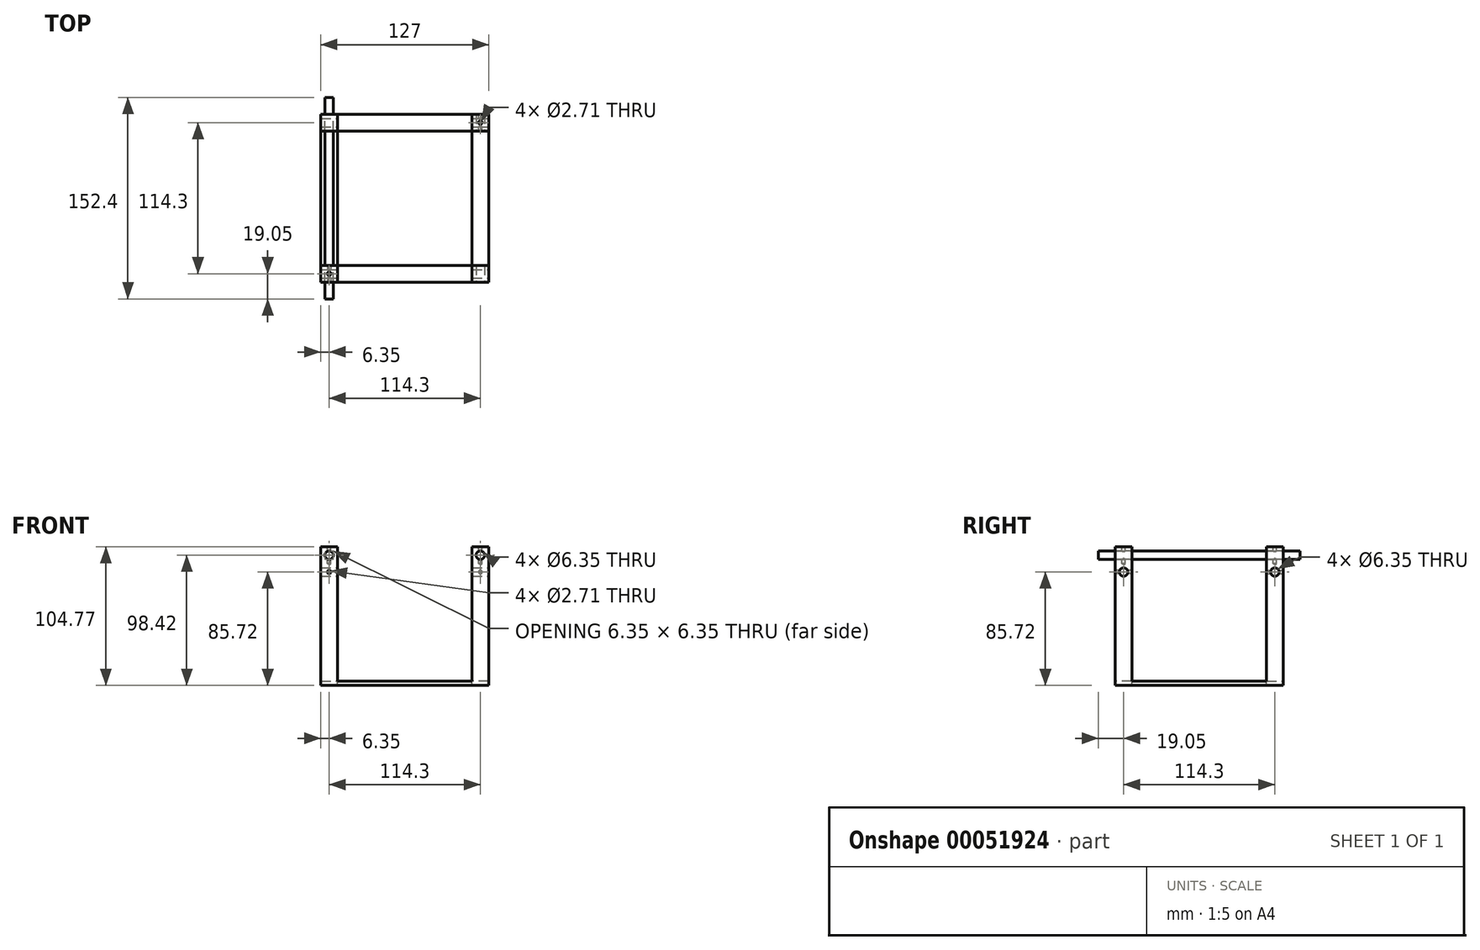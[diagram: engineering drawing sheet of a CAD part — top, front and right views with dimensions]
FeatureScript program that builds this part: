
annotation { "Feature Type Name" : "Feature", "Feature Type Description" : "" }
export const myFeature = defineFeature(function(context is Context, id is Id, definition is map)
    precondition{}
    {
        {
            var Q0;
            Q0=qCreatedBy(makeId("Top.planeOp"),FACE);
            var sketch = newSketch(context, id + "F0", { "sketchPlane" : qUnion([Q0])});
            skLineSegment(sketch, "E0.bottom", {"start": v(57.15, -57.15) * mm, "end": v(-57.15, -57.15) * mm, "construction": true});
            skLineSegment(sketch, "E0.top", {"start": v(57.15, 57.15) * mm, "end": v(-57.15, 57.15) * mm, "construction": true});
            skLineSegment(sketch, "E0.left", {"start": v(57.15, -57.15) * mm, "end": v(57.15, 57.15) * mm, "construction": true});
            skLineSegment(sketch, "E0.right", {"start": v(-57.15, -57.15) * mm, "end": v(-57.15, 57.15) * mm, "construction": true});
            skPoint(sketch, "E0.middle", {"position": v(0, 0) * mm});
            skLineSegment(sketch, "E1.bottom", {"start": v(-50.8, 50.8) * mm, "end": v(-63.5, 50.8) * mm});
            skLineSegment(sketch, "E1.top", {"start": v(-50.8, 63.5) * mm, "end": v(-63.5, 63.5) * mm});
            skLineSegment(sketch, "E1.left", {"start": v(-50.8, 50.8) * mm, "end": v(-50.8, 63.5) * mm});
            skLineSegment(sketch, "E1.right", {"start": v(-63.5, 50.8) * mm, "end": v(-63.5, 63.5) * mm});
            skPoint(sketch, "E1.middle", {"position": v(-57.15, 57.15) * mm});
            skLineSegment(sketch, "E2.bottom", {"start": v(63.5, 50.8) * mm, "end": v(50.8, 50.8) * mm});
            skLineSegment(sketch, "E2.top", {"start": v(63.5, 63.5) * mm, "end": v(50.8, 63.5) * mm});
            skLineSegment(sketch, "E2.left", {"start": v(63.5, 50.8) * mm, "end": v(63.5, 63.5) * mm});
            skLineSegment(sketch, "E2.right", {"start": v(50.8, 50.8) * mm, "end": v(50.8, 63.5) * mm});
            skPoint(sketch, "E2.middle", {"position": v(57.15, 57.15) * mm});
            skLineSegment(sketch, "E3.bottom", {"start": v(63.5, -50.8) * mm, "end": v(50.8, -50.8) * mm});
            skLineSegment(sketch, "E3.top", {"start": v(63.5, -63.5) * mm, "end": v(50.8, -63.5) * mm});
            skLineSegment(sketch, "E3.left", {"start": v(63.5, -50.8) * mm, "end": v(63.5, -63.5) * mm});
            skLineSegment(sketch, "E3.right", {"start": v(50.8, -50.8) * mm, "end": v(50.8, -63.5) * mm});
            skPoint(sketch, "E3.middle", {"position": v(57.15, -57.15) * mm});
            skLineSegment(sketch, "E4.bottom", {"start": v(-63.5, -50.8) * mm, "end": v(-50.8, -50.8) * mm});
            skLineSegment(sketch, "E4.top", {"start": v(-63.5, -63.5) * mm, "end": v(-50.8, -63.5) * mm});
            skLineSegment(sketch, "E4.left", {"start": v(-63.5, -50.8) * mm, "end": v(-63.5, -63.5) * mm});
            skLineSegment(sketch, "E4.right", {"start": v(-50.8, -50.8) * mm, "end": v(-50.8, -63.5) * mm});
            skPoint(sketch, "E4.middle", {"position": v(-57.15, -57.15) * mm});
            skLineSegment(sketch, "E5", {"start": v(-50.8, 63.5) * mm, "end": v(50.8, 63.5) * mm});
            skLineSegment(sketch, "E6", {"start": v(-50.8, 50.8) * mm, "end": v(50.8, 50.8) * mm});
            skLineSegment(sketch, "E7", {"start": v(50.8, 50.8) * mm, "end": v(50.8, -50.8) * mm});
            skLineSegment(sketch, "E8", {"start": v(63.5, 50.8) * mm, "end": v(63.5, -50.8) * mm});
            skLineSegment(sketch, "E9", {"start": v(50.8, -50.8) * mm, "end": v(-50.8, -50.8) * mm});
            skLineSegment(sketch, "E10", {"start": v(50.8, -63.5) * mm, "end": v(-50.8, -63.5) * mm});
            skLineSegment(sketch, "E11", {"start": v(-50.8, -50.8) * mm, "end": v(-50.8, 50.8) * mm});
            skLineSegment(sketch, "E12", {"start": v(-63.5, -50.8) * mm, "end": v(-63.5, 50.8) * mm});
            skSolve(sketch);
        }
        {
            var Q0;
            Q0=makeQuery(id+"F0.imprint","IMPRINT",FACE,{"disambiguationData":[TD([[makeQuery(id+"F0.imprint","IMPRINT",EDGE,{"derivedFrom":sQuery(id+"F0.wireOp",EDGE,"E4.bottom")}),-1.0]])]});
            var Q1;
            Q1=makeQuery(id+"F0.imprint","IMPRINT",FACE,{"disambiguationData":[TD([[makeQuery(id+"F0.imprint","IMPRINT",EDGE,{"derivedFrom":sQuery(id+"F0.wireOp",EDGE,"E1.bottom")}),1.0]])]});
            var Q2;
            Q2=makeQuery(id+"F0.imprint","IMPRINT",FACE,{"disambiguationData":[TD([[makeQuery(id+"F0.imprint","IMPRINT",EDGE,{"derivedFrom":sQuery(id+"F0.wireOp",EDGE,"E1.bottom")}),-1.0]])]});
            var Q3;
            Q3=makeQuery(id+"F0.imprint","IMPRINT",FACE,{"disambiguationData":[TD([[makeQuery(id+"F0.imprint","IMPRINT",EDGE,{"derivedFrom":sQuery(id+"F0.wireOp",EDGE,"E1.left")}),-1.0]])]});
            var Q4;
            Q4=makeQuery(id+"F0.imprint","IMPRINT",FACE,{"disambiguationData":[TD([[makeQuery(id+"F0.imprint","IMPRINT",EDGE,{"derivedFrom":sQuery(id+"F0.wireOp",EDGE,"E2.bottom")}),-1.0]])]});
            var Q5;
            Q5=makeQuery(id+"F0.imprint","IMPRINT",FACE,{"disambiguationData":[TD([[makeQuery(id+"F0.imprint","IMPRINT",EDGE,{"derivedFrom":sQuery(id+"F0.wireOp",EDGE,"E2.bottom")}),1.0]])]});
            var Q6;
            Q6=makeQuery(id+"F0.imprint","IMPRINT",FACE,{"disambiguationData":[TD([[makeQuery(id+"F0.imprint","IMPRINT",EDGE,{"derivedFrom":sQuery(id+"F0.wireOp",EDGE,"E3.bottom")}),1.0]])]});
            var Q7;
            Q7=makeQuery(id+"F0.imprint","IMPRINT",FACE,{"disambiguationData":[TD([[makeQuery(id+"F0.imprint","IMPRINT",EDGE,{"derivedFrom":sQuery(id+"F0.wireOp",EDGE,"E3.right")}),-1.0]])]});
            extrude(context, id + "F1", {"entities" : qUnion([Q0, Q1, Q2, Q3, Q4, Q5, Q6, Q7]), "oppositeDirection" : true, "depth" : 3.17 * mm});
        }
        {
            var Q0;
            Q0=makeQuery(id+"F0.imprint","IMPRINT",FACE,{"disambiguationData":[TD([[makeQuery(id+"F0.imprint","IMPRINT",EDGE,{"derivedFrom":sQuery(id+"F0.wireOp",EDGE,"E4.bottom")}),-1.0]])]});
            var Q1;
            Q1=makeQuery(id+"F0.imprint","IMPRINT",FACE,{"disambiguationData":[TD([[makeQuery(id+"F0.imprint","IMPRINT",EDGE,{"derivedFrom":sQuery(id+"F0.wireOp",EDGE,"E1.bottom")}),-1.0]])]});
            var Q2;
            Q2=makeQuery(id+"F0.imprint","IMPRINT",FACE,{"disambiguationData":[TD([[makeQuery(id+"F0.imprint","IMPRINT",EDGE,{"derivedFrom":sQuery(id+"F0.wireOp",EDGE,"E2.bottom")}),-1.0]])]});
            var Q3;
            Q3=makeQuery(id+"F0.imprint","IMPRINT",FACE,{"disambiguationData":[TD([[makeQuery(id+"F0.imprint","IMPRINT",EDGE,{"derivedFrom":sQuery(id+"F0.wireOp",EDGE,"E3.bottom")}),1.0]])]});
            extrude(context, id + "F2", {"entities" : qUnion([Q0, Q1, Q2, Q3]), "operationType" : NewBodyOperationType.ADD, "depth" : 101.6 * mm});
        }
        {
            var Q0;
            {var subQ0=sQuery(id+"F0.wireOp",EDGE,"E4.top");var subQ1=sQuery(id+"F0.wireOp",EDGE,"E3.top");Q0=makeQuery(id+"F2.boolean.opBoolean","MERGE",FACE,{"derivedFrom":[makeQuery(id+"F1.opExtrude","SWEPT_FACE",FACE,{"disambiguationData":[OSD([subQ1,subQ0,sQuery(id+"F0.wireOp",EDGE,"E10")])]}),makeQuery(id+"F2.opExtrude","SWEPT_FACE",FACE,{"disambiguationData":[OSD([subQ1])]}),makeQuery(id+"F2.opExtrude","SWEPT_FACE",FACE,{"disambiguationData":[OSD([subQ0])]})]});}
            var sketch = newSketch(context, id + "F3", { "sketchPlane" : qUnion([Q0])});
            skLineSegment(sketch, "E13.0.0", {"start": v(50.8, 0) * mm, "end": v(-50.8, 0) * mm, "construction": true});
            skLineSegment(sketch, "E13.0.1", {"start": v(-50.8, 0) * mm, "end": v(-50.8, 101.6) * mm, "construction": true});
            skLineSegment(sketch, "E13.0.2", {"start": v(-50.8, 101.6) * mm, "end": v(-63.5, 101.6) * mm, "construction": true});
            skLineSegment(sketch, "E13.0.3", {"start": v(-63.5, 101.6) * mm, "end": v(-63.5, -3.18) * mm, "construction": true});
            skLineSegment(sketch, "E13.0.4", {"start": v(-63.5, -3.18) * mm, "end": v(63.5, -3.18) * mm, "construction": true});
            skLineSegment(sketch, "E13.0.5", {"start": v(63.5, -3.18) * mm, "end": v(63.5, 101.6) * mm, "construction": true});
            skLineSegment(sketch, "E13.0.6", {"start": v(63.5, 101.6) * mm, "end": v(50.8, 101.6) * mm, "construction": true});
            skLineSegment(sketch, "E13.0.7", {"start": v(50.8, 101.6) * mm, "end": v(50.8, 0) * mm, "construction": true});
            skLineSegment(sketch, "E14", {"start": v(-57.15, 101.6) * mm, "end": v(-57.15, -3.17) * mm, "construction": true});
            skLineSegment(sketch, "E15", {"start": v(57.15, 101.6) * mm, "end": v(57.15, -3.17) * mm, "construction": true});
            skCircle(sketch, "E16", {"center": v(-57.15, 95.25) * mm, "radius": 3.18 * mm});
            skCircle(sketch, "E17", {"center": v(57.15, 95.25) * mm, "radius": 3.18 * mm});
            skSolve(sketch);
        }
        {
            var Q0;
            Q0 = qSketchRegion(id + "F3", true);
            extrude(context, id + "F4", {"entities" : qUnion([Q0]), "operationType" : NewBodyOperationType.REMOVE, "endBound" : BoundingType.THROUGH_ALL, "oppositeDirection" : true, "depth" : 25.4 * mm});
        }
        {
            var Q0;
            {var subQ0=sQuery(id+"F0.wireOp",EDGE,"E3.left");var subQ1=sQuery(id+"F0.wireOp",EDGE,"E2.left");Q0=makeQuery(id+"F2.boolean.opBoolean","MERGE",FACE,{"derivedFrom":[makeQuery(id+"F1.opExtrude","SWEPT_FACE",FACE,{"disambiguationData":[OSD([subQ1,subQ0,sQuery(id+"F0.wireOp",EDGE,"E8")])]}),makeQuery(id+"F2.opExtrude","SWEPT_FACE",FACE,{"disambiguationData":[OSD([subQ1])]}),makeQuery(id+"F2.opExtrude","SWEPT_FACE",FACE,{"disambiguationData":[OSD([subQ0])]})]});}
            var sketch = newSketch(context, id + "F5", { "sketchPlane" : qUnion([Q0])});
            skLineSegment(sketch, "E18.0.0", {"start": v(50.8, 0) * mm, "end": v(-50.8, 0) * mm, "construction": true});
            skLineSegment(sketch, "E18.0.1", {"start": v(-50.8, 0) * mm, "end": v(-50.8, 101.6) * mm, "construction": true});
            skLineSegment(sketch, "E18.0.2", {"start": v(-50.8, 101.6) * mm, "end": v(-63.5, 101.6) * mm, "construction": true});
            skLineSegment(sketch, "E18.0.3", {"start": v(-63.5, 101.6) * mm, "end": v(-63.5, -3.18) * mm, "construction": true});
            skLineSegment(sketch, "E18.0.4", {"start": v(-63.5, -3.18) * mm, "end": v(63.5, -3.18) * mm, "construction": true});
            skLineSegment(sketch, "E18.0.5", {"start": v(63.5, -3.18) * mm, "end": v(63.5, 101.6) * mm, "construction": true});
            skLineSegment(sketch, "E18.0.6", {"start": v(63.5, 101.6) * mm, "end": v(50.8, 101.6) * mm, "construction": true});
            skLineSegment(sketch, "E18.0.7", {"start": v(50.8, 101.6) * mm, "end": v(50.8, 0) * mm, "construction": true});
            skLineSegment(sketch, "E19", {"start": v(-57.15, 101.6) * mm, "end": v(-57.15, -3.17) * mm, "construction": true});
            skLineSegment(sketch, "E20", {"start": v(57.15, 101.6) * mm, "end": v(57.15, -3.17) * mm, "construction": true});
            skCircle(sketch, "E21", {"center": v(-57.15, 82.55) * mm, "radius": 3.18 * mm});
            skCircle(sketch, "E22", {"center": v(57.15, 82.55) * mm, "radius": 3.18 * mm});
            skSolve(sketch);
        }
        {
            var Q0;
            Q0=makeQuery(id+"F5.imprint","IMPRINT",FACE,{"disambiguationData":[TD([[makeQuery(id+"F5.imprint","IMPRINT",EDGE,{"derivedFrom":sQuery(id+"F5.wireOp",EDGE,"E21")}),1.0]])]});
            var Q1;
            Q1=makeQuery(id+"F5.imprint","IMPRINT",FACE,{"disambiguationData":[TD([[makeQuery(id+"F5.imprint","IMPRINT",EDGE,{"derivedFrom":sQuery(id+"F5.wireOp",EDGE,"E22")}),1.0]])]});
            extrude(context, id + "F6", {"entities" : qUnion([Q0, Q1]), "operationType" : NewBodyOperationType.REMOVE, "endBound" : BoundingType.THROUGH_ALL, "oppositeDirection" : true, "depth" : 25.4 * mm});
        }
        {
            var Q0;
            Q0=makeQuery(id+"F2.opExtrude","CAP_FACE",FACE,{"disambiguationData":[OSD([sQuery(id+"F0.wireOp",EDGE,"E4.bottom"),sQuery(id+"F0.wireOp",EDGE,"E4.top"),sQuery(id+"F0.wireOp",EDGE,"E4.left"),sQuery(id+"F0.wireOp",EDGE,"E4.right")])],"isStart":false});
            var sketch = newSketch(context, id + "F7", { "sketchPlane" : qUnion([Q0])});
            skLineSegment(sketch, "E23.0.0", {"start": v(50.8, 50.8) * mm, "end": v(63.5, 50.8) * mm, "construction": true});
            skLineSegment(sketch, "E23.0.1", {"start": v(63.5, 50.8) * mm, "end": v(63.5, 63.5) * mm, "construction": true});
            skLineSegment(sketch, "E23.0.2", {"start": v(63.5, 63.5) * mm, "end": v(50.8, 63.5) * mm, "construction": true});
            skLineSegment(sketch, "E23.0.3", {"start": v(50.8, 63.5) * mm, "end": v(50.8, 50.8) * mm, "construction": true});
            skLineSegment(sketch, "E24.0.0", {"start": v(-50.8, -50.8) * mm, "end": v(-63.5, -50.8) * mm, "construction": true});
            skLineSegment(sketch, "E24.0.1", {"start": v(-63.5, -50.8) * mm, "end": v(-63.5, -63.5) * mm, "construction": true});
            skLineSegment(sketch, "E24.0.2", {"start": v(-63.5, -63.5) * mm, "end": v(-50.8, -63.5) * mm, "construction": true});
            skLineSegment(sketch, "E24.0.3", {"start": v(-50.8, -63.5) * mm, "end": v(-50.8, -50.8) * mm, "construction": true});
            skLineSegment(sketch, "E25", {"start": v(50.8, 50.8) * mm, "end": v(63.5, 63.5) * mm, "construction": true});
            skLineSegment(sketch, "E26", {"start": v(-63.5, -63.5) * mm, "end": v(-50.8, -50.8) * mm, "construction": true});
            skPoint(sketch, "E27", {"position": v(57.15, 57.15) * mm});
            skPoint(sketch, "E28", {"position": v(-57.15, -57.15) * mm});
            skSolve(sketch);
        }
        {
            var Q0;
            {var subQ0=sQuery(id+"F0.wireOp",EDGE,"E4.top");var subQ1=sQuery(id+"F0.wireOp",EDGE,"E3.top");Q0=makeQuery(id+"F2.boolean.opBoolean","MERGE",FACE,{"derivedFrom":[makeQuery(id+"F1.opExtrude","SWEPT_FACE",FACE,{"disambiguationData":[OSD([subQ1,subQ0,sQuery(id+"F0.wireOp",EDGE,"E10")])]}),makeQuery(id+"F2.opExtrude","SWEPT_FACE",FACE,{"disambiguationData":[OSD([subQ1])]}),makeQuery(id+"F2.opExtrude","SWEPT_FACE",FACE,{"disambiguationData":[OSD([subQ0])]})]});}
            var sketch = newSketch(context, id + "F8", { "sketchPlane" : qUnion([Q0])});
            skLineSegment(sketch, "E29", {"start": v(-57.15, 101.6) * mm, "end": v(-57.15, -3.17) * mm, "construction": true});
            skPoint(sketch, "E30", {"position": v(-57.15, 82.55) * mm});
            skSolve(sketch);
        }
        {
            var Q0;
            {var subQ0=sQuery(id+"F0.wireOp",EDGE,"E2.top");var subQ1=sQuery(id+"F0.wireOp",EDGE,"E1.top");Q0=makeQuery(id+"F2.boolean.opBoolean","MERGE",FACE,{"derivedFrom":[makeQuery(id+"F1.opExtrude","SWEPT_FACE",FACE,{"disambiguationData":[OSD([subQ1,subQ0,sQuery(id+"F0.wireOp",EDGE,"E5")])]}),makeQuery(id+"F2.opExtrude","SWEPT_FACE",FACE,{"disambiguationData":[OSD([subQ1])]}),makeQuery(id+"F2.opExtrude","SWEPT_FACE",FACE,{"disambiguationData":[OSD([subQ0])]})]});}
            var sketch = newSketch(context, id + "F9", { "sketchPlane" : qUnion([Q0])});
            skLineSegment(sketch, "E31", {"start": v(-57.15, 101.6) * mm, "end": v(-57.15, -3.17) * mm, "construction": true});
            skPoint(sketch, "E32", {"position": v(-57.15, 82.55) * mm});
            skSolve(sketch);
        }
        {
            var Q0;
            Q0=sQuery(id+"F7.wireOp",VERTEX,"E28");
            var Q1;
            Q1=sQuery(id+"F7.wireOp",VERTEX,"E27");
            var Q2;
            Q2=sQuery(id+"F8.wireOp",VERTEX,"E30");
            var Q3;
            Q3=sQuery(id+"F9.wireOp",VERTEX,"E32");
            var Q4;
            Q4=makeQuery(id+"F1.opExtrude","SWEPT_BODY",BODY,{"disambiguationData":[OSD([sQuery(id+"F0.wireOp",EDGE,"E1.top"),sQuery(id+"F0.wireOp",EDGE,"E1.right"),sQuery(id+"F0.wireOp",EDGE,"E2.top"),sQuery(id+"F0.wireOp",EDGE,"E2.left"),sQuery(id+"F0.wireOp",EDGE,"E3.top"),sQuery(id+"F0.wireOp",EDGE,"E3.left"),sQuery(id+"F0.wireOp",EDGE,"E4.top"),sQuery(id+"F0.wireOp",EDGE,"E4.left"),sQuery(id+"F0.wireOp",EDGE,"E5"),sQuery(id+"F0.wireOp",EDGE,"E6"),sQuery(id+"F0.wireOp",EDGE,"E7"),sQuery(id+"F0.wireOp",EDGE,"E8"),sQuery(id+"F0.wireOp",EDGE,"E9"),sQuery(id+"F0.wireOp",EDGE,"E10"),sQuery(id+"F0.wireOp",EDGE,"E11"),sQuery(id+"F0.wireOp",EDGE,"E12")])]});
            hole(context, id + "F10", {"style" : HoleStyle.SIMPLE, "endStyle" : HoleEndStyle.BLIND, "standardTappedOrClearance" : lookupTablePath({ "standard" : "ANSI", "engagement" : "75%", "pitch" : "32 tpi", "size" : "#6", "type" : "Tapped" }), "standardBlindInLast" : lookupTablePath({ "standard" : "ANSI", "engagement" : "75%", "pitch" : "32 tpi", "size" : "#6", "type" : "Tapped" }), "holeDiameter" : 2.7 * mm, "holeDepth" : 12.7 * mm, "locations" : qUnion([Q0, Q1, Q2, Q3]), "scope" : qUnion([Q4]), "majorDiameter" : 3.5 * mm});
        }
        {
            var Q0;
            {var subQ0=sQuery(id+"F0.wireOp",EDGE,"E4.top");var subQ1=sQuery(id+"F0.wireOp",EDGE,"E3.top");Q0=makeQuery(id+"F2.boolean.opBoolean","MERGE",FACE,{"derivedFrom":[makeQuery(id+"F1.opExtrude","SWEPT_FACE",FACE,{"disambiguationData":[OSD([subQ1,subQ0,sQuery(id+"F0.wireOp",EDGE,"E10")])]}),makeQuery(id+"F2.opExtrude","SWEPT_FACE",FACE,{"disambiguationData":[OSD([subQ1])]}),makeQuery(id+"F2.opExtrude","SWEPT_FACE",FACE,{"disambiguationData":[OSD([subQ0])]})]});}
            var sketch = newSketch(context, id + "F11", { "sketchPlane" : qUnion([Q0])});
            skCircle(sketch, "E33.0", {"center": v(-57.15, 95.25) * mm, "radius": 3.18 * mm});
            skSolve(sketch);
        }
        {
            var Q0;
            Q0=makeQuery(id+"F11.imprint","IMPRINT",FACE,{"disambiguationData":[TD([[makeQuery(id+"F11.imprint","IMPRINT",EDGE,{"derivedFrom":sQuery(id+"F11.wireOp",EDGE,"E33.0")}),1.0]])]});
            extrude(context, id + "F12", {"entities" : qUnion([Q0]), "depth" : 12.7 * mm, "hasSecondDirection" : true, "secondDirectionOppositeDirection" : true, "secondDirectionDepth" : 139.7 * mm});
        }
    });
